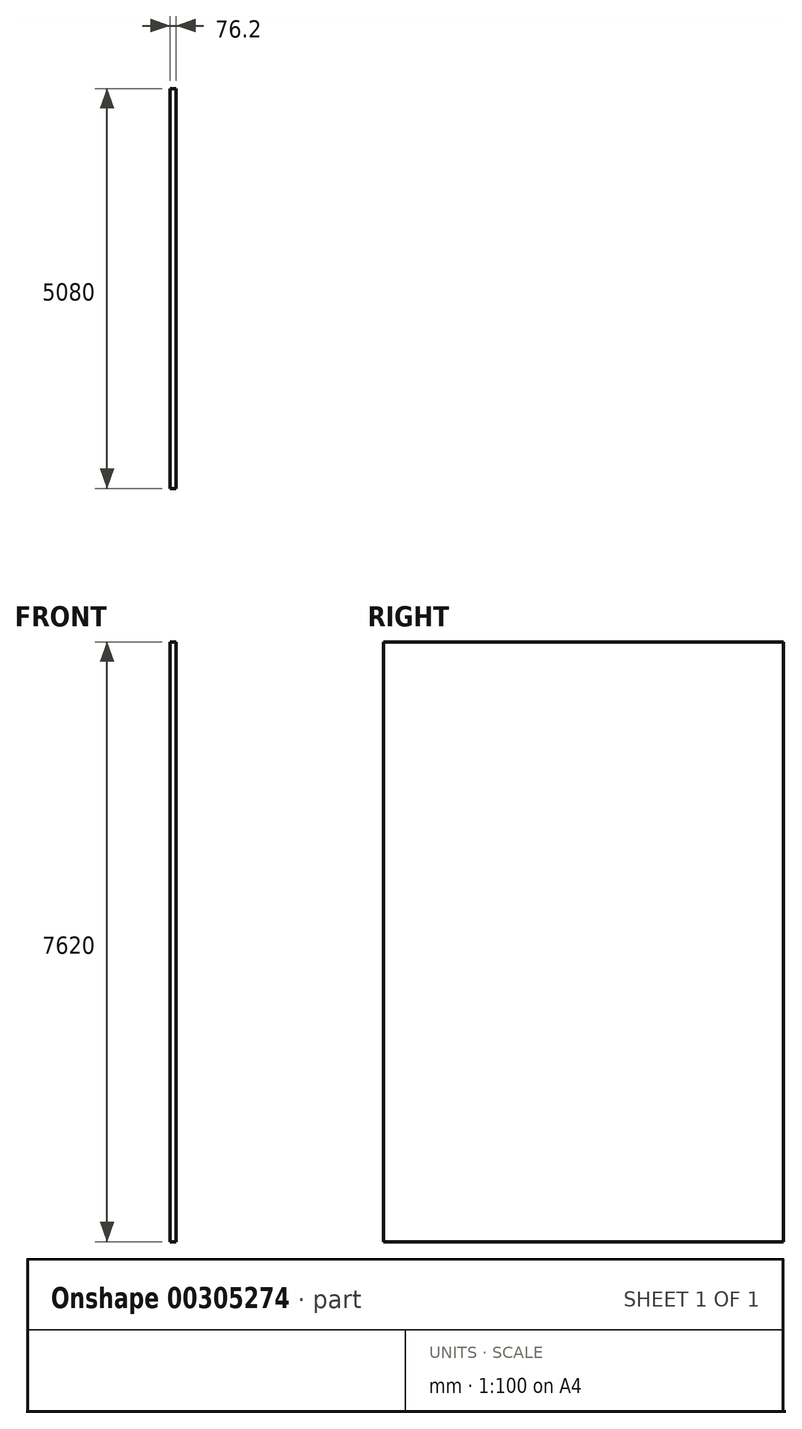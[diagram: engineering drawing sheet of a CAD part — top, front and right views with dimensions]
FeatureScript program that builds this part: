
annotation { "Feature Type Name" : "Feature", "Feature Type Description" : "" }
export const myFeature = defineFeature(function(context is Context, id is Id, definition is map)
    precondition{}
    {
        {
            var Q0;
            Q0=qCreatedBy(makeId("Top.planeOp"),FACE);
            var sketch = newSketch(context, id + "F0", { "sketchPlane" : qUnion([Q0])});
            skLineSegment(sketch, "E0.bottom", {"start": v(-38.1, 2540) * mm, "end": v(38.1, 2540) * mm});
            skLineSegment(sketch, "E0.top", {"start": v(-38.1, -2540) * mm, "end": v(38.1, -2540) * mm});
            skLineSegment(sketch, "E0.left", {"start": v(-38.1, 2540) * mm, "end": v(-38.1, -2540) * mm});
            skLineSegment(sketch, "E0.right", {"start": v(38.1, 2540) * mm, "end": v(38.1, -2540) * mm});
            skLineSegment(sketch, "E1", {"start": v(0, 0) * mm, "end": v(0, 48306.94) * mm, "construction": true});
            skLineSegment(sketch, "E2", {"start": v(0, 0) * mm, "end": v(30507.47, 0) * mm, "construction": true});
            skSolve(sketch);
        }
        {
            var Q0;
            Q0 = qSketchRegion(id + "F0", true);
            extrude(context, id + "F1", {"entities" : qUnion([Q0]), "depth" : 7620 * mm});
        }
    });
